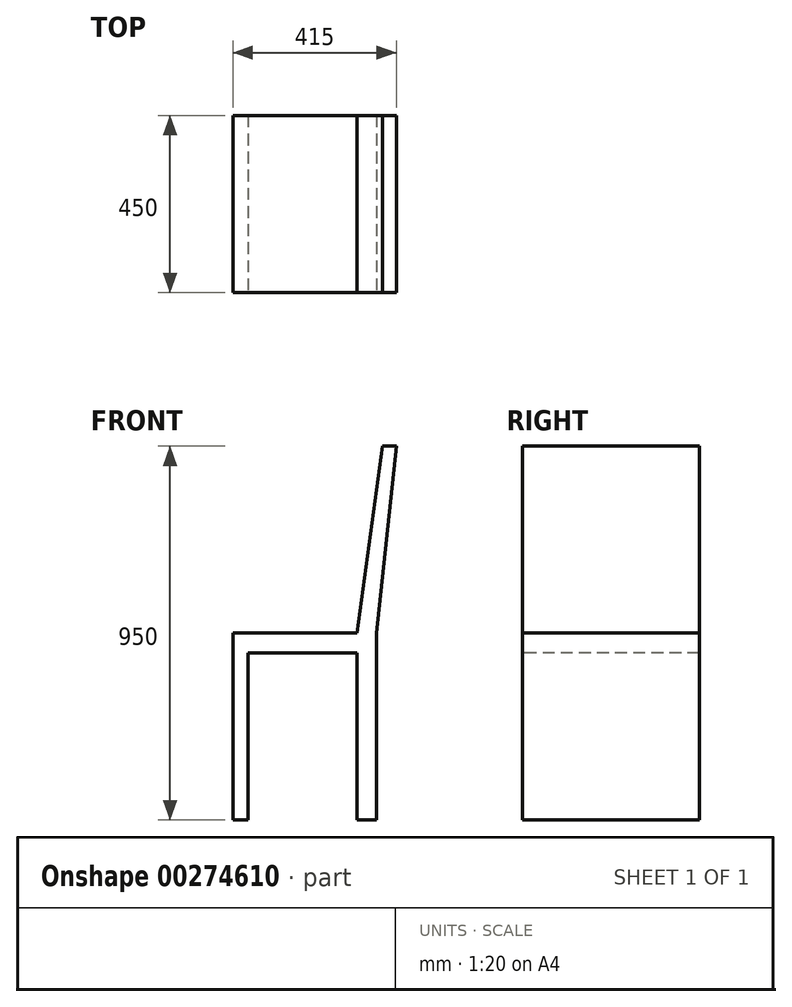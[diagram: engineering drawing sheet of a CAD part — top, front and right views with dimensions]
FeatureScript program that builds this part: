
annotation { "Feature Type Name" : "Feature", "Feature Type Description" : "" }
export const myFeature = defineFeature(function(context is Context, id is Id, definition is map)
    precondition{}
    {
        {
            var Q0;
            Q0=qCreatedBy(makeId("Top.planeOp"),FACE);
            var sketch = newSketch(context, id + "F0", { "sketchPlane" : qUnion([Q0])});
            skLineSegment(sketch, "E0.bottom", {"start": v(225, 225) * mm, "end": v(-225, 225) * mm});
            skLineSegment(sketch, "E0.top", {"start": v(225, -225) * mm, "end": v(-225, -225) * mm});
            skLineSegment(sketch, "E0.left", {"start": v(225, 225) * mm, "end": v(225, -225) * mm});
            skLineSegment(sketch, "E0.right", {"start": v(-225, 225) * mm, "end": v(-225, -225) * mm});
            skPoint(sketch, "E0.middle", {"position": v(0, 0) * mm});
            skSolve(sketch);
        }
        {
            var Q0;
            Q0=qSketchRegion(id+"F0",true);
            extrude(context, id + "F1", {"entities" : qUnion([Q0]), "depth" : 950 * mm});
        }
        {
            var Q0;
            Q0=makeQuery(id+"F1.opExtrude","SWEPT_FACE",FACE,{"disambiguationData":[OSD([sQuery(id+"F0.wireOp",EDGE,"E0.top")])]});
            var sketch = newSketch(context, id + "F2", { "sketchPlane" : qUnion([Q0])});
            skLineSegment(sketch, "E1.bottom", {"start": v(-225, 475) * mm, "end": v(225, 475) * mm});
            skLineSegment(sketch, "E1.top", {"start": v(-225, 425) * mm, "end": v(225, 425) * mm});
            skLineSegment(sketch, "E1.left", {"start": v(-225, 475) * mm, "end": v(-225, 425) * mm});
            skLineSegment(sketch, "E1.right", {"start": v(225, 475) * mm, "end": v(225, 425) * mm});
            skLineSegment(sketch, "E2", {"start": v(225, 950) * mm, "end": v(175, 475) * mm});
            skLineSegment(sketch, "E3", {"start": v(190, 950) * mm, "end": v(125.14, 475) * mm});
            skLineSegment(sketch, "E4", {"start": v(175, 475) * mm, "end": v(175, 0) * mm});
            skLineSegment(sketch, "E5", {"start": v(125.14, 475) * mm, "end": v(125.14, 0) * mm});
            skLineSegment(sketch, "E6", {"start": v(-190, 425) * mm, "end": v(-190, 0) * mm});
            skLineSegment(sketch, "E7", {"start": v(-152.1, 425) * mm, "end": v(-152.1, 0) * mm});
            skLineSegment(sketch, "E8", {"start": v(-190, 425) * mm, "end": v(-190, 475) * mm});
            skSolve(sketch);
        }
        {
            var Q0;
            {var subQ6=sQuery(id+"F2.wireOp",EDGE,"E3");Q0=makeQuery(id+"F2.imprint","IMPRINT",FACE,{"disambiguationData":[TD([[makeQuery(id+"F2.imprint","IMPRINT",EDGE,{"derivedFrom":subQ6}),-1.0]])]});}
            var Q1;
            {var subQ0=sQuery(id+"F2.wireOp",EDGE,"E1.left");Q1=makeQuery(id+"F2.imprint","IMPRINT",FACE,{"disambiguationData":[TD([[makeQuery(id+"F2.imprint","IMPRINT",EDGE,{"derivedFrom":subQ0}),1.0]])]});}
            var Q2;
            {var subQ4=sQuery(id+"F2.wireOp",EDGE,"E6");Q2=makeQuery(id+"F2.imprint","IMPRINT",FACE,{"disambiguationData":[TD([[makeQuery(id+"F2.imprint","IMPRINT",EDGE,{"derivedFrom":subQ4}),-1.0]])]});}
            var Q3;
            {var subQ0=sQuery(id+"F2.wireOp",EDGE,"E7");Q3=makeQuery(id+"F2.imprint","IMPRINT",FACE,{"disambiguationData":[TD([[makeQuery(id+"F2.imprint","IMPRINT",EDGE,{"derivedFrom":subQ0}),1.0]])]});}
            var Q4;
            {var subQ1=sQuery(id+"F0.wireOp",EDGE,"E0.top");var subQ4=sQuery(id+"F2.wireOp",EDGE,"E4");var subQ6=makeQuery(id+"F1.opExtrude","CAP_EDGE",EDGE,{"disambiguationData":[OSD([subQ1])],"isStart":true});var subQ8=makeQuery(id+"F2.imprint","INTERSECT",VERTEX,{"derivedFrom":[subQ6,subQ4]});Q4=makeQuery(id+"F2.imprint","IMPRINT",FACE,{"disambiguationData":[TD([[makeQuery(id+"F2.imprint","IMPRINT",EDGE,{"disambiguationData":[TD([[subQ8,1.0]])],"derivedFrom":subQ4}),1.0]])]});}
            var Q5;
            {var subQ4=sQuery(id+"F2.wireOp",EDGE,"E2");Q5=makeQuery(id+"F2.imprint","IMPRINT",FACE,{"disambiguationData":[TD([[makeQuery(id+"F2.imprint","IMPRINT",EDGE,{"derivedFrom":subQ4}),1.0]])]});}
            var Q6;
            {var subQ0=sQuery(id+"F2.wireOp",EDGE,"E1.right");Q6=makeQuery(id+"F2.imprint","IMPRINT",FACE,{"disambiguationData":[TD([[makeQuery(id+"F2.imprint","IMPRINT",EDGE,{"derivedFrom":subQ0}),-1.0]])]});}
            extrude(context, id + "F3", {"entities" : qUnion([Q0, Q1, Q2, Q3, Q4, Q5, Q6]), "operationType" : NewBodyOperationType.REMOVE, "endBound" : BoundingType.THROUGH_ALL, "oppositeDirection" : true, "depth" : 25 * mm});
        }
    });
